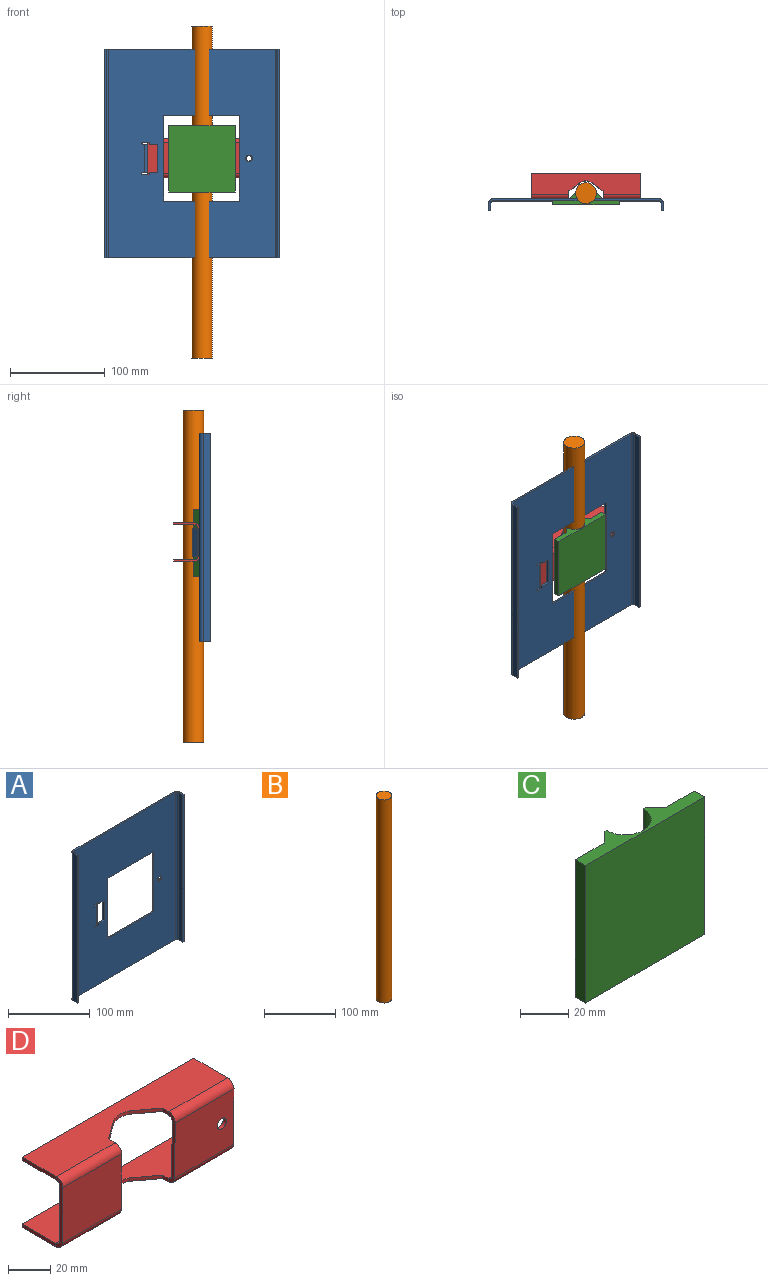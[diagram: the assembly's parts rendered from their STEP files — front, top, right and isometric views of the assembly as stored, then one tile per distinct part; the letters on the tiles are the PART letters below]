
ASSEMBLY  parts=4 mates=3
PART A: 47 faces, bbox 184x18.5x220 mm
  f0: plane 9.29x2mm, normal (0,0,1), area 18.6mm2, adj f1,f2,f3,f15
  f1: plane 220x175.4mm, normal (0,1,0), area 30904.6mm2, adj f0,f3,f4,f5,f6,f7,f8,f9
  f2: plane 220x175.4mm, normal (0,-1,0), area 30904.6mm2, adj f0,f3,f4,f5,f6,f7,f8,f9
  f3: plane 30x2mm, normal (-1,0,0), area 60mm2, adj f0,f1,f2,f11
  f4: plane 90x2mm, normal (1,0,0), area 180mm2, adj f1,f2,f5,f10
  f5: plane 80x2mm, normal (0,0,1), area 160mm2, adj f1,f2,f4,f6
  f6: plane 90x2mm, normal (-1,0,0), area 180mm2, adj f1,f2,f5,f10
  f7: plane 175.4x2mm, normal (0,0,-1), area 350.8mm2, adj f1,f2,f26,f35
  f8: plane 175.4x2mm, normal (0,0,1), area 350.8mm2, adj f1,f2,f25,f34
  f9: cylinder r=3.4mm len=6.8mm, axis (0,1,0), area 42.7mm2, adj f1,f2
  f10: plane 80x2mm, normal (0,0,-1), area 160mm2, adj f1,f2,f4,f6
  f11: plane 9.29x2mm, normal (0,0,-1), area 18.6mm2, adj f1,f2,f3,f19
  f12: plane 6.9x2mm, normal (0,0,1), area 13.8mm2, adj f1,f2,f13,f15
  f13: cylinder r=1.06mm len=2.13mm, axis (0,-1,0), area 6.7mm2, adj f1,f2,f12,f14
  f14: plane 2.39x2mm, normal (0,0,-1), area 4.8mm2, adj f1,f2,f13,f43
  f15: plane 2.13x2mm, normal (-1,0,0), area 4.3mm2, adj f0,f1,f2,f12
  f16: plane 2.39x2mm, normal (0,0,1), area 4.8mm2, adj f1,f2,f17,f44
  f17: cylinder r=1.06mm len=2.13mm, axis (0,-1,0), area 6.7mm2, adj f1,f2,f16,f18
  f18: plane 6.9x2mm, normal (0,0,-1), area 13.8mm2, adj f1,f2,f17,f19
  f19: plane 2.13x2mm, normal (-1,0,0), area 4.3mm2, adj f1,f2,f11,f18
  f20: plane 7.7x2mm, normal (0,0,-1), area 15.4mm2, adj f22,f23,f24,f26
  f21: plane 7.7x2mm, normal (0,0,1), area 15.4mm2, adj f22,f23,f24,f25
  f22: plane 220x2mm, normal (0,-1,0), area 440mm2, adj f20,f21,f23,f24
  f23: plane 220x7.7mm, normal (1,0,0), area 1694mm2, adj f20,f21,f22,f27
  f24: plane 220x7.7mm, normal (-1,0,0), area 1694mm2, adj f20,f21,f22,f28
  f25: plane 4.3x4.3mm, normal (0,0,1), area 10.4mm2, adj f8,f21,f27,f28
  f26: plane 4.3x4.3mm, normal (0,0,-1), area 10.4mm2, adj f7,f20,f27,f28
  f27: cylinder r=4.3mm len=220mm, axis (0,0,1), area 1486mm2, adj f1,f23,f25,f26
  f28: cylinder r=2.3mm len=220mm, axis (0,0,1), area 794.8mm2, adj f2,f24,f25,f26
  f29: plane 7.7x2mm, normal (0,0,-1), area 15.4mm2, adj f30,f32,f33,f35
  f30: plane 220x2mm, normal (0,-1,0), area 440mm2, adj f29,f31,f32,f33
  f31: plane 7.7x2mm, normal (0,0,1), area 15.4mm2, adj f30,f32,f33,f34
  f32: plane 220x7.7mm, normal (-1,0,0), area 1694mm2, adj f29,f30,f31,f36
  f33: plane 220x7.7mm, normal (1,0,0), area 1694mm2, adj f29,f30,f31,f37
  f34: plane 4.3x4.3mm, normal (0,0,1), area 10.4mm2, adj f8,f31,f36,f37
  f35: plane 4.3x4.3mm, normal (0,0,-1), area 10.4mm2, adj f7,f29,f36,f37
  f36: cylinder r=4.3mm len=220mm, axis (0,0,1), area 1486mm2, adj f1,f32,f34,f35
  f37: cylinder r=2.3mm len=220mm, axis (0,0,1), area 794.8mm2, adj f2,f33,f34,f35
  f38: plane 30x1.41mm, normal (0.71,0.71,0), area 60mm2, adj f39,f40,f41,f42
  f39: plane 7.23x7.23mm, normal (0,0,-1), area 16.4mm2, adj f38,f41,f42,f43
  f40: plane 7.23x7.23mm, normal (0,0,1), area 16.4mm2, adj f38,f41,f42,f44
  f41: plane 30x5.81mm, normal (-0.71,0.71,0), area 246.6mm2, adj f38,f39,f40,f46
  f42: plane 30x5.81mm, normal (0.71,-0.71,0), area 246.6mm2, adj f38,f39,f40,f45
  f43: plane 3.04x2.67mm, normal (0,0,-1), area 5.2mm2, adj f14,f39,f45,f46
  f44: plane 3.04x2.67mm, normal (0,0,1), area 5.2mm2, adj f16,f40,f45,f46
  f45: cylinder r=4.3mm len=30mm, axis (0,0,-1), area 101.3mm2, adj f2,f42,f43,f44
  f46: cylinder r=2.3mm len=30mm, axis (0,0,-1), area 54.2mm2, adj f1,f41,f43,f44
PART B: 3 faces, bbox 22x22x350 mm
  f0: cylinder r=11mm len=350mm, axis (0,0,-1), area 24190.3mm2, adj f1,f2
  f1: plane 22x22mm, normal (0,0,1), area 380.1mm2, adj f0
  f2: plane 22x22mm, normal (0,0,-1), area 380.1mm2, adj f0
PART C: 12 faces, bbox 70x12x70 mm
  f0: plane 70x17mm, normal (0,1,0), area 1190mm2, adj f1,f9,f10,f11
  f1: plane 70x6mm, normal (-1,0,0), area 420mm2, adj f0,f2,f10,f11
  f2: plane 70x70mm, normal (0,-1,0), area 4900mm2, adj f1,f3,f10,f11
  f3: plane 70x6mm, normal (1,0,0), area 420mm2, adj f2,f4,f10,f11
  f4: plane 70x17mm, normal (0,1,0), area 1190mm2, adj f3,f5,f10,f11
  f5: plane 70x6mm, normal (0.71,0.71,0), area 594mm2, adj f4,f6,f10,f11
  f6: plane 70x1mm, normal (0,1,0), area 70mm2, adj f5,f7,f10,f11
  f7: cylinder r=11mm len=70mm, axis (0,0,-1), area 2419mm2, adj f6,f8,f10,f11
  f8: plane 70x1mm, normal (0,1,0), area 70mm2, adj f7,f9,f10,f11
  f9: plane 70x6mm, normal (-0.71,0.71,0), area 594mm2, adj f0,f8,f10,f11
  f10: plane 70x12mm, normal (0,0,1), area 409.9mm2, adj f0,f1,f2,f3,f4,f5,f6,f7
  f11: plane 70x12mm, normal (0,0,-1), area 409.9mm2, adj f0,f1,f2,f3,f4,f5,f6,f7
PART D: 45 faces, bbox 115x27.3x41 mm
  f0: plane 12.53x9.25mm, normal (0.59,-0.8,0), area 31.1mm2, adj f1,f7,f8,f9
  f1: cylinder r=11.5mm len=10.94mm, axis (0,0,1), area 22.8mm2, adj f0,f2,f8,f9
  f2: plane 12.53x9.25mm, normal (-0.59,-0.8,0), area 31.1mm2, adj f1,f3,f8,f9
  f3: plane 4.32x2mm, normal (-1,0,0), area 8.6mm2, adj f2,f8,f9,f42
  f4: plane 22.68x2mm, normal (1,0,0), area 45.4mm2, adj f5,f8,f9,f41
  f5: plane 115x2mm, normal (0,1,0), area 230mm2, adj f4,f6,f8,f9
  f6: plane 22.68x2mm, normal (-1,0,0), area 45.4mm2, adj f5,f8,f9,f29
  f7: plane 4.32x2mm, normal (1,0,0), area 8.6mm2, adj f0,f8,f9,f28
  f8: plane 115x22.68mm, normal (0,0,1), area 2225.1mm2, adj f0,f1,f2,f3,f4,f5,f6,f7
  f9: plane 115x22.68mm, normal (0,0,-1), area 2225.1mm2, adj f0,f1,f2,f3,f4,f5,f6,f7
  f10: plane 12.53x9.25mm, normal (-0.59,-0.8,0), area 31.1mm2, adj f11,f17,f18,f19
  f11: cylinder r=11.5mm len=10.94mm, axis (0,0,-1), area 22.8mm2, adj f10,f12,f18,f19
  f12: plane 12.53x9.25mm, normal (0.59,-0.8,0), area 31.1mm2, adj f11,f13,f18,f19
  f13: plane 4x2mm, normal (1,0,0), area 8mm2, adj f12,f18,f19,f24
  f14: plane 22.72x2mm, normal (-1,0,0), area 45.4mm2, adj f15,f18,f19,f25
  f15: plane 115x2mm, normal (0,1,0), area 230mm2, adj f14,f16,f18,f19
  f16: plane 22.72x2mm, normal (1,0,0), area 45.4mm2, adj f15,f18,f19,f37
  f17: plane 4x2mm, normal (-1,0,0), area 8mm2, adj f10,f18,f19,f38
  f18: plane 115x22.72mm, normal (0,0,-1), area 2241.7mm2, adj f10,f11,f12,f13,f14,f15,f16,f17
  f19: plane 115x22.72mm, normal (0,0,1), area 2241.7mm2, adj f10,f11,f12,f13,f14,f15,f16,f17
  f20: plane 32.42x2.32mm, normal (-1,0,0), area 64.8mm2, adj f22,f23,f25,f29
  f21: plane 32.42x2.32mm, normal (1,0,0), area 64.8mm2, adj f22,f23,f24,f28
  f22: plane 39.5x32.4mm, normal (0,-1,-0.01), area 1279.8mm2, adj f20,f21,f26,f30
  f23: plane 39.5x32.4mm, normal (0,1,0.01), area 1279.8mm2, adj f20,f21,f27,f31
  f24: plane 4.3x4.28mm, normal (1,0,0), area 10.3mm2, adj f13,f21,f26,f27
  f25: plane 4.3x4.28mm, normal (-1,0,0), area 10.3mm2, adj f14,f20,f26,f27
  f26: cylinder r=4.3mm len=39.5mm, axis (1,0,0), area 265.1mm2, adj f18,f22,f24,f25
  f27: cylinder r=2.3mm len=39.5mm, axis (1,0,0), area 141.8mm2, adj f19,f23,f24,f25
  f28: plane 4.34x4.3mm, normal (1,0,0), area 10.4mm2, adj f7,f21,f30,f31
  f29: plane 4.34x4.3mm, normal (-1,0,0), area 10.4mm2, adj f6,f20,f30,f31
  f30: cylinder r=4.3mm len=39.5mm, axis (1,0,0), area 268.5mm2, adj f8,f22,f28,f29
  f31: cylinder r=2.3mm len=39.5mm, axis (1,0,0), area 143.6mm2, adj f9,f23,f28,f29
  f32: plane 32.42x2.32mm, normal (1,0,0), area 64.8mm2, adj f35,f36,f37,f41
  f33: cylinder r=3mm len=6.02mm, axis (0,-1,-0.01), area 37.7mm2, adj f35,f36
  f34: plane 32.42x2.32mm, normal (-1,0,0), area 64.8mm2, adj f35,f36,f38,f42
  f35: plane 39.5x32.4mm, normal (0,-1,-0.01), area 1251.5mm2, adj f32,f33,f34,f39,f43
  f36: plane 39.5x32.4mm, normal (0,1,0.01), area 1251.5mm2, adj f32,f33,f34,f40,f44
  f37: plane 4.3x4.28mm, normal (1,0,0), area 10.3mm2, adj f16,f32,f39,f40
  f38: plane 4.3x4.28mm, normal (-1,0,0), area 10.3mm2, adj f17,f34,f39,f40
  f39: cylinder r=4.3mm len=39.5mm, axis (1,0,0), area 265.1mm2, adj f18,f35,f37,f38
  f40: cylinder r=2.3mm len=39.5mm, axis (1,0,0), area 141.8mm2, adj f19,f36,f37,f38
  f41: plane 4.34x4.3mm, normal (1,0,0), area 10.4mm2, adj f4,f32,f43,f44
  f42: plane 4.34x4.3mm, normal (-1,0,0), area 10.4mm2, adj f3,f34,f43,f44
  f43: cylinder r=4.3mm len=39.5mm, axis (1,0,0), area 268.5mm2, adj f8,f35,f41,f42
  f44: cylinder r=2.3mm len=39.5mm, axis (1,0,0), area 143.6mm2, adj f9,f36,f41,f42
PLACE A t=(-97.97,-35.77,3.75)mm fixed
PLACE B t=(-177.47,-27.77,-101.75)mm
PLACE C t=(-169.66,-45.47,73.25)mm
PLACE D rot(axis=(-1,0,0),0.6deg) t=(-234.93,-19.27,108.76)mm
MATE fastened B.f0 <-> C.f7  axis (0,0,-1) through (-177.47,-27.77,73.25)mm
MATE planar C.f0 <-> A.f1  axis (0,1,0) through (-203.97,-33.77,108.25)mm
MATE planar D.f22 <-> C.f0  axis (0,-1,0) through (-215.18,-33.77,108.86)mm
